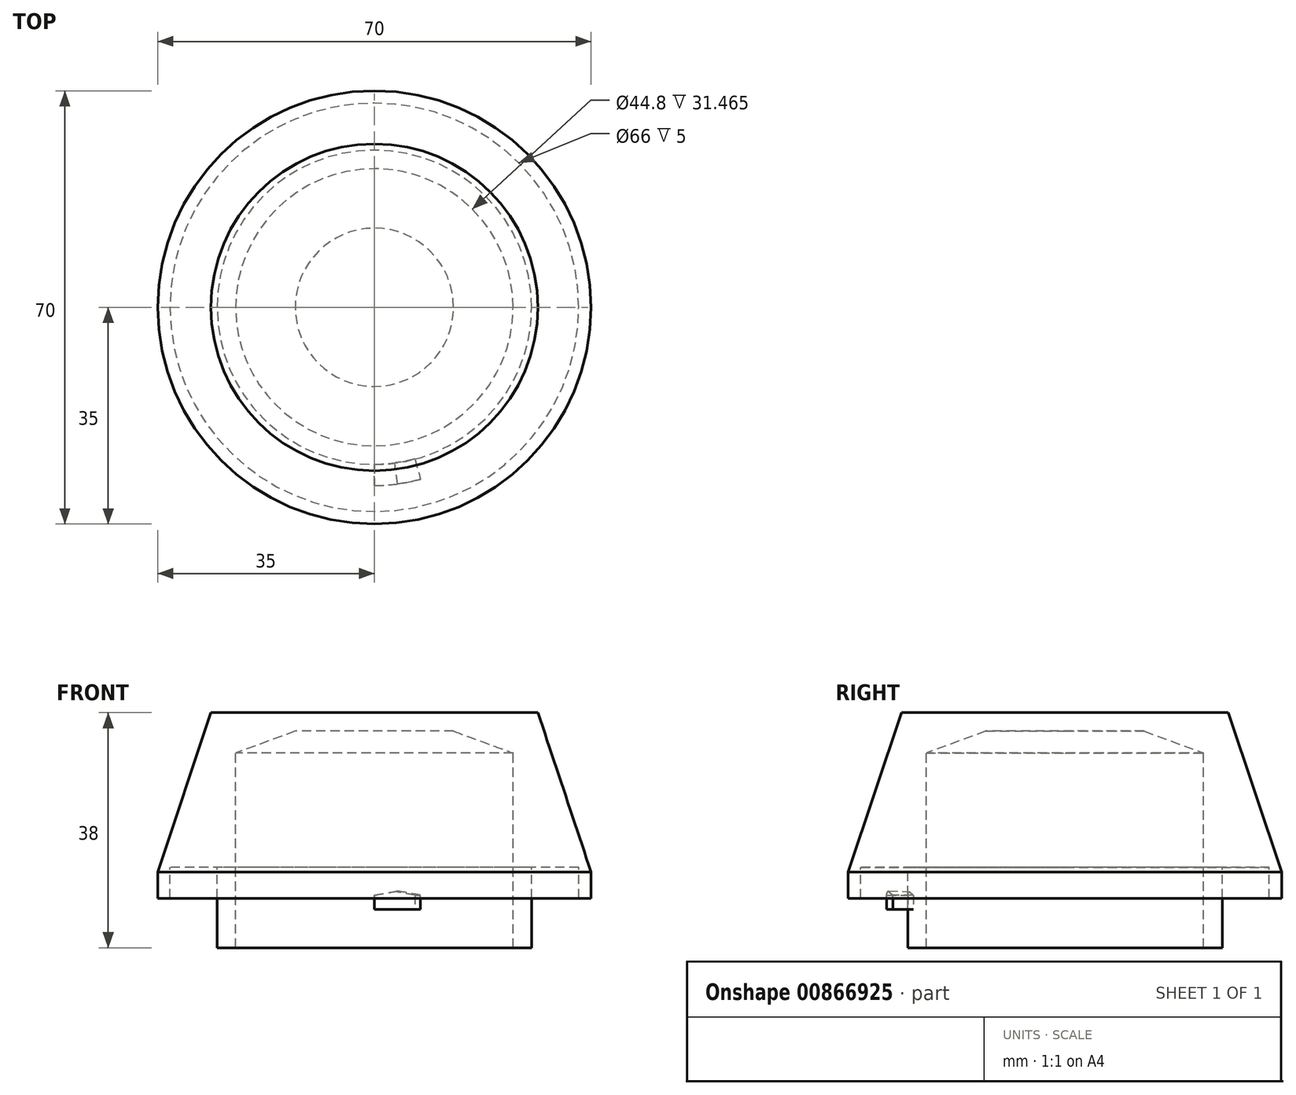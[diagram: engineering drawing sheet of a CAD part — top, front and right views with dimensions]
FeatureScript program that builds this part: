
annotation { "Feature Type Name" : "Feature", "Feature Type Description" : "" }
export const myFeature = defineFeature(function(context is Context, id is Id, definition is map)
    precondition{}
    {
        {
            var Q0;
            Q0=qCreatedBy(makeId("Front.planeOp"),FACE);
            var sketch = newSketch(context, id + "F0", { "sketchPlane" : qUnion([Q0])});
            skLineSegment(sketch, "E0", {"start": v(-25.4, 0) * mm, "end": v(-25.4, 13) * mm});
            skLineSegment(sketch, "E1", {"start": v(-25.4, 13) * mm, "end": v(-33, 13) * mm});
            skLineSegment(sketch, "E2", {"start": v(-33, 13) * mm, "end": v(-33, 8) * mm});
            skLineSegment(sketch, "E3", {"start": v(-33, 8) * mm, "end": v(-35, 8) * mm});
            skLineSegment(sketch, "E4", {"start": v(-35, 8) * mm, "end": v(-35, 12.23) * mm});
            skLineSegment(sketch, "E5", {"start": v(-35, 12.23) * mm, "end": v(-26.41, 38) * mm});
            skLineSegment(sketch, "E6", {"start": v(-26.41, 38) * mm, "end": v(0, 38) * mm});
            skLineSegment(sketch, "E7", {"start": v(-25.4, 0) * mm, "end": v(-22.4, 0) * mm});
            skLineSegment(sketch, "E8", {"start": v(-22.4, 0) * mm, "end": v(-22.4, 31.46) * mm});
            skLineSegment(sketch, "E9", {"start": v(-22.4, 31.46) * mm, "end": v(-12.79, 35) * mm});
            skLineSegment(sketch, "E10", {"start": v(-12.79, 35) * mm, "end": v(0, 35) * mm});
            skLineSegment(sketch, "E11", {"start": v(0, 35) * mm, "end": v(0, 38) * mm});
            skSolve(sketch);
        }
        {
            var Q0;
            Q0=qCreatedBy(makeId("Front.planeOp"),FACE);
            var sketch = newSketch(context, id + "F1", { "sketchPlane" : qUnion([Q0])});
            skLineSegment(sketch, "E12", {"start": v(0, 165.48) * mm, "end": v(0, -161.4) * mm, "construction": true});
            skSolve(sketch);
        }
        {
            var Q0;
            Q0 = qSketchRegion(id + "F0", true);
            var Q1;
            Q1=sQuery(id+"F1.wireOp",EDGE,"E12");
            revolve(context, id + "F2", {"surfaceOperationType" : NewSurfaceOperationType.NEW, "entities" : qUnion([Q0]), "axis" : qUnion([Q1]), "revolveType" : RevolveType.FULL});
        }
        {
            var Q0;
            Q0=qCreatedBy(makeId("Right.planeOp"),FACE);
            var sketch = newSketch(context, id + "F3", { "sketchPlane" : qUnion([Q0])});
            skLineSegment(sketch, "E13", {"start": v(-25.36, 6.2) * mm, "end": v(-28.8, 6.2) * mm});
            skLineSegment(sketch, "E14", {"start": v(-28.8, 6.2) * mm, "end": v(-28.8, 9.2) * mm});
            skLineSegment(sketch, "E15", {"start": v(-28.8, 9.2) * mm, "end": v(-25.36, 9.2) * mm});
            skLineSegment(sketch, "E16", {"start": v(-25.36, 9.2) * mm, "end": v(-25.36, 6.2) * mm});
            skSolve(sketch);
        }
        {
            var Q0;
            Q0 = qSketchRegion(id + "F3", true);
            var Q1;
            Q1=makeQuery(id+"F2.opRevolve","SWEPT_FACE",FACE,{"disambiguationData":[OSD([sQuery(id+"F0.wireOp",EDGE,"E8")])]});
            revolve(context, id + "F4", {"surfaceOperationType" : NewSurfaceOperationType.NEW, "entities" : qUnion([Q0]), "axis" : qUnion([Q1]), "revolveType" : RevolveType.ONE_DIRECTION, "oppositeDirection" : true, "angle" : 15 * degree});
        }
        {
            var Q0;
            Q0=makeQuery(id+"F4.opRevolve","CAP_EDGE",EDGE,{"disambiguationData":[OSD([sQuery(id+"F3.wireOp",EDGE,"E15")])],"isStart":true});
            var Q1;
            Q1=makeQuery(id+"F4.opRevolve","CAP_EDGE",EDGE,{"disambiguationData":[OSD([sQuery(id+"F3.wireOp",EDGE,"E15")])],"isStart":false});
            chamfer(context, id + "F5", {"entities" : qUnion([Q0, Q1]), "chamferType" : ChamferType.OFFSET_ANGLE, "width" : .7 * mm, "oppositeDirection" : false, "angle" : 80 * degree, "tangentPropagation" : true});
        }
    });
